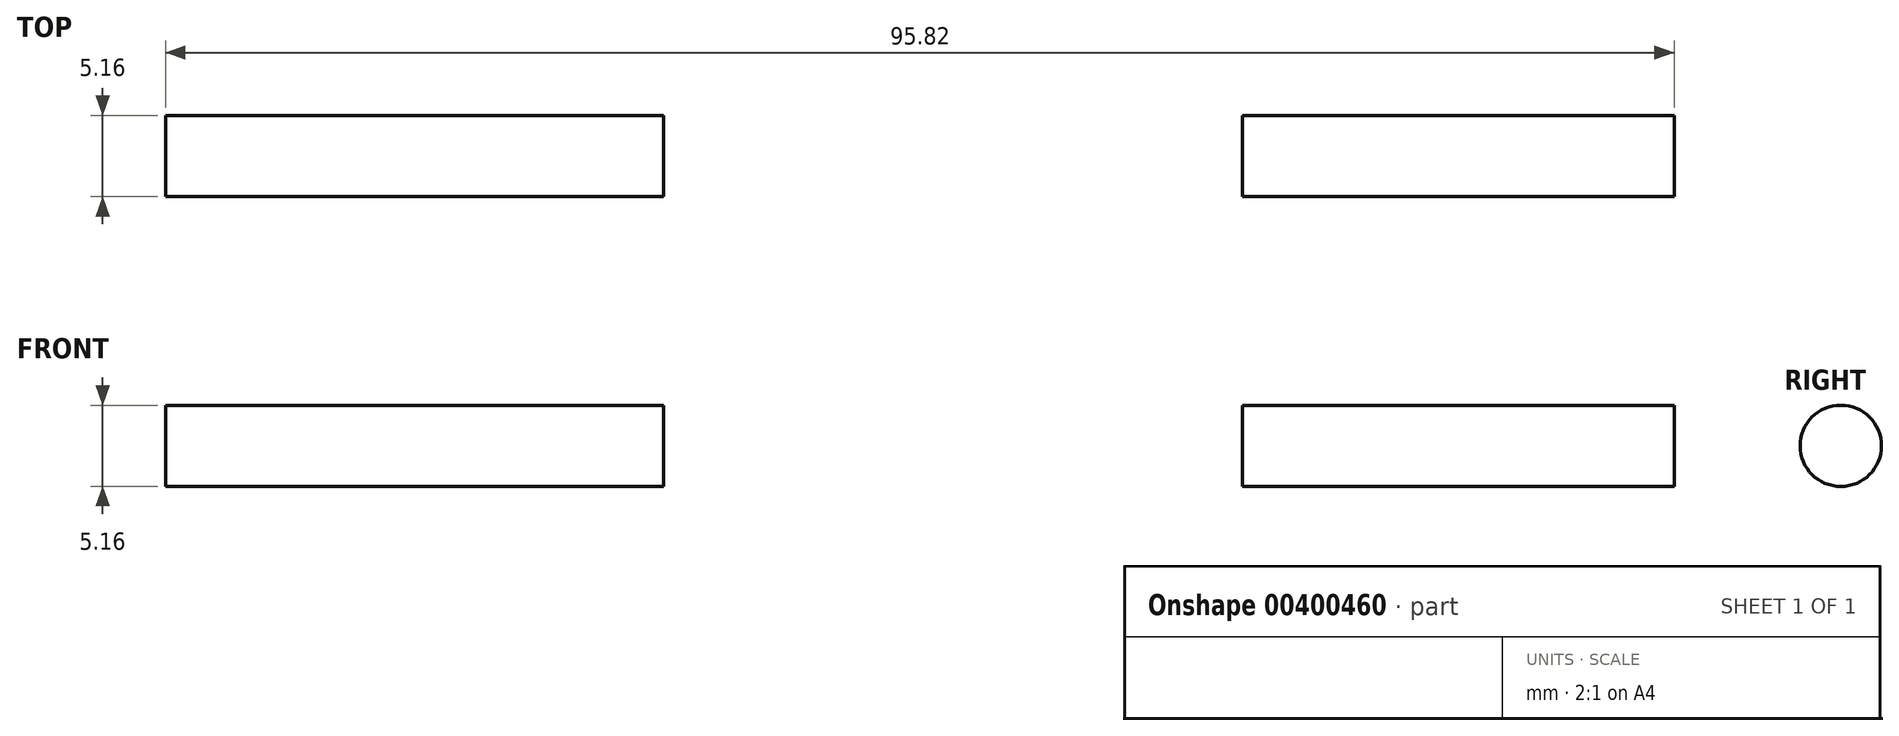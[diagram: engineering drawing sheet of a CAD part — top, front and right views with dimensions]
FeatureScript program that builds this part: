
annotation { "Feature Type Name" : "Feature", "Feature Type Description" : "" }
export const myFeature = defineFeature(function(context is Context, id is Id, definition is map)
    precondition{}
    {
        {
            var Q0;
            Q0=qCreatedBy(makeId("Front.planeOp"),FACE);
            var sketch = newSketch(context, id + "F0", { "sketchPlane" : qUnion([Q0])});
            skLineSegment(sketch, "E0.bottom", {"start": v(-12.58, 0) * mm, "end": v(-44.2, 0) * mm});
            skLineSegment(sketch, "E0.top", {"start": v(-12.58, 2.58) * mm, "end": v(-44.2, 2.58) * mm});
            skLineSegment(sketch, "E0.left", {"start": v(-12.58, 0) * mm, "end": v(-12.58, 2.58) * mm});
            skLineSegment(sketch, "E0.right", {"start": v(-44.2, 0) * mm, "end": v(-44.2, 2.58) * mm});
            skLineSegment(sketch, "E1.bottom", {"start": v(24.2, 0) * mm, "end": v(51.62, 0) * mm});
            skLineSegment(sketch, "E1.top", {"start": v(24.2, 2.58) * mm, "end": v(51.62, 2.58) * mm});
            skLineSegment(sketch, "E1.left", {"start": v(24.2, 0) * mm, "end": v(24.2, 2.58) * mm});
            skLineSegment(sketch, "E1.right", {"start": v(51.62, 0) * mm, "end": v(51.62, 2.58) * mm});
            skLineSegment(sketch, "E2.bottom", {"start": v(44.84, 2.58) * mm, "end": v(46.46, 2.58) * mm});
            skLineSegment(sketch, "E2.top", {"start": v(44.84, 9.03) * mm, "end": v(46.46, 9.03) * mm});
            skLineSegment(sketch, "E3.bottom", {"start": v(-38.07, 0) * mm, "end": v(-36.13, 0) * mm});
            skLineSegment(sketch, "E3.top", {"start": v(-38.07, 9.03) * mm, "end": v(-36.13, 9.03) * mm});
            skSolve(sketch);
        }
        {
            var Q0;
            Q0 = qSketchRegion(id + "F0", true);
            var Q1;
            Q1=sQuery(id+"F0.wireOp",EDGE,"E0.bottom");
            revolve(context, id + "F1", {"entities" : qUnion([Q0]), "axis" : qUnion([Q1]), "revolveType" : RevolveType.FULL});
        }
    });
